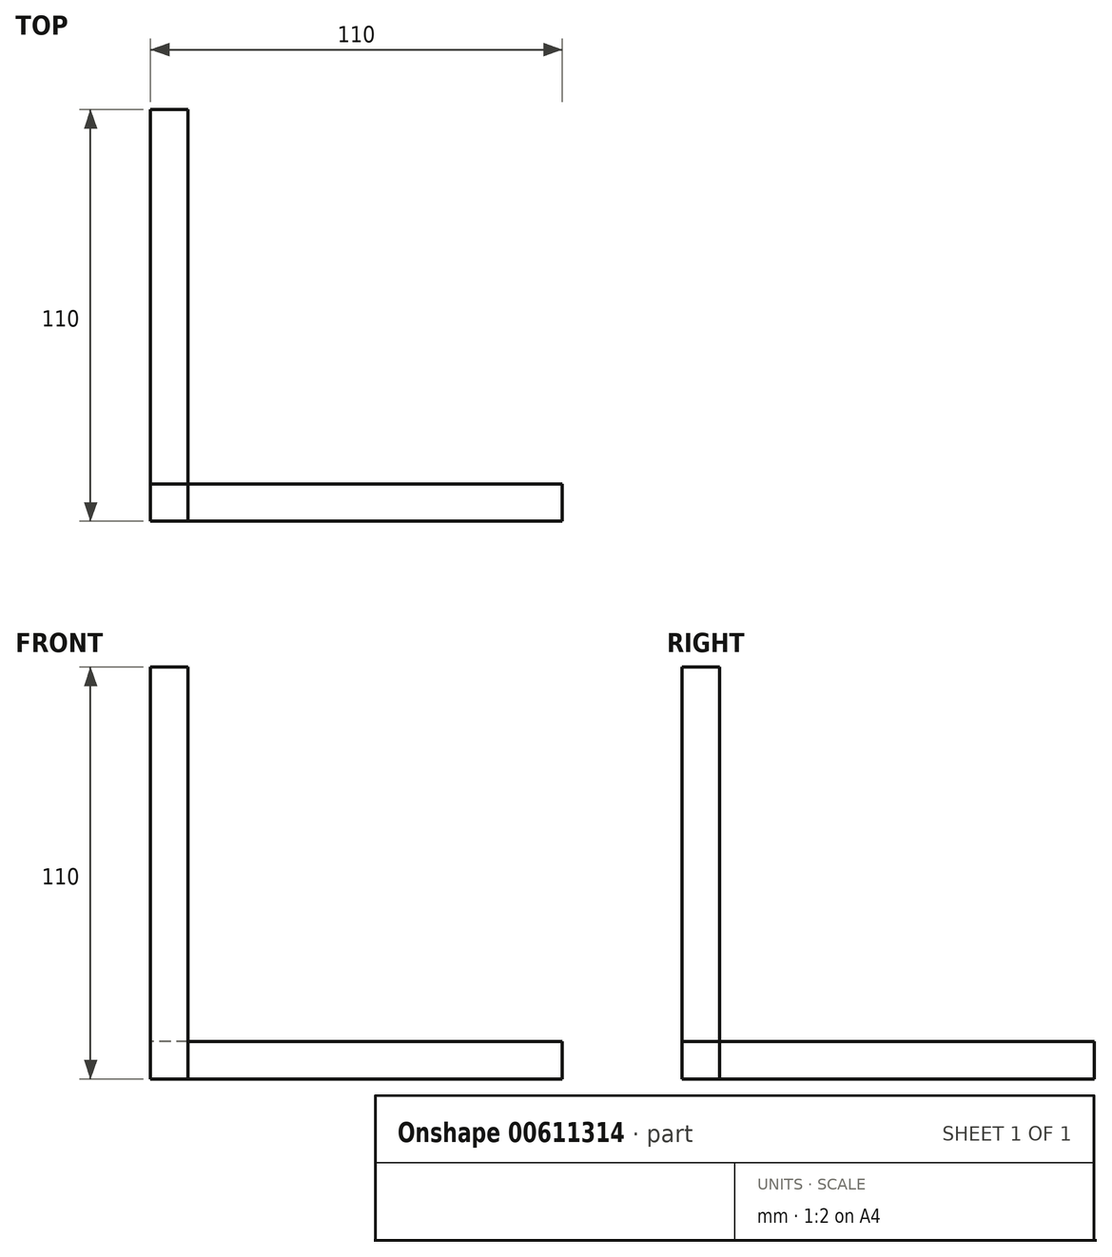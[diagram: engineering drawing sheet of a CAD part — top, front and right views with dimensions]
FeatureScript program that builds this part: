
annotation { "Feature Type Name" : "Feature", "Feature Type Description" : "" }
export const myFeature = defineFeature(function(context is Context, id is Id, definition is map)
    precondition{}
    {
        {
            var Q0;
            Q0=qCreatedBy(makeId("Top.planeOp"),FACE);
            var sketch = newSketch(context, id + "F0", { "sketchPlane" : qUnion([Q0])});
            skLineSegment(sketch, "E0.bottom", {"start": v(0, 0) * mm, "end": v(-10, 0) * mm});
            skLineSegment(sketch, "E0.top", {"start": v(0, 100) * mm, "end": v(-10, 100) * mm});
            skLineSegment(sketch, "E0.left", {"start": v(0, 0) * mm, "end": v(0, 100) * mm});
            skLineSegment(sketch, "E0.right", {"start": v(-10, 0) * mm, "end": v(-10, 100) * mm});
            skSolve(sketch);
        }
        {
            var Q0;
            Q0=makeQuery(id+"F0.imprint","IMPRINT",FACE,{"disambiguationData":[TD([[makeQuery(id+"F0.imprint","IMPRINT",EDGE,{"derivedFrom":sQuery(id+"F0.wireOp",EDGE,"E0.bottom")}),-1.0]])]});
            extrude(context, id + "F1", {"entities" : qUnion([Q0]), "depth" : 10 * mm, "offsetDistance" : 25 * mm});
        }
        {
            var Q0;
            Q0=qCreatedBy(makeId("Top.planeOp"),FACE);
            var sketch = newSketch(context, id + "F2", { "sketchPlane" : qUnion([Q0])});
            skLineSegment(sketch, "E1.bottom", {"start": v(0, 0) * mm, "end": v(100, 0) * mm});
            skLineSegment(sketch, "E1.top", {"start": v(0, -10) * mm, "end": v(100, -10) * mm});
            skLineSegment(sketch, "E1.left", {"start": v(0, 0) * mm, "end": v(0, -10) * mm});
            skLineSegment(sketch, "E1.right", {"start": v(100, 0) * mm, "end": v(100, -10) * mm});
            skSolve(sketch);
        }
        {
            var Q0;
            Q0=makeQuery(id+"F2.imprint","IMPRINT",FACE,{"disambiguationData":[TD([[makeQuery(id+"F2.imprint","IMPRINT",EDGE,{"derivedFrom":sQuery(id+"F2.wireOp",EDGE,"E1.bottom")}),-1.0]])]});
            extrude(context, id + "F3", {"entities" : qUnion([Q0]), "depth" : 10 * mm, "offsetDistance" : 25 * mm});
        }
        {
            var Q0;
            Q0=qCreatedBy(makeId("Front.planeOp"),FACE);
            var sketch = newSketch(context, id + "F4", { "sketchPlane" : qUnion([Q0])});
            skLineSegment(sketch, "E2.bottom", {"start": v(0, 0) * mm, "end": v(-10, 0) * mm});
            skLineSegment(sketch, "E2.top", {"start": v(0, 110) * mm, "end": v(-10, 110) * mm});
            skLineSegment(sketch, "E2.left", {"start": v(0, 0) * mm, "end": v(0, 110) * mm});
            skLineSegment(sketch, "E2.right", {"start": v(-10, 0) * mm, "end": v(-10, 110) * mm});
            skSolve(sketch);
        }
        {
            var Q0;
            Q0=makeQuery(id+"F4.imprint","IMPRINT",FACE,{"disambiguationData":[TD([[makeQuery(id+"F4.imprint","IMPRINT",EDGE,{"derivedFrom":sQuery(id+"F4.wireOp",EDGE,"E2.bottom")}),-1.0]])]});
            extrude(context, id + "F5", {"entities" : qUnion([Q0]), "depth" : 10 * mm, "offsetDistance" : 25 * mm});
        }
    });
